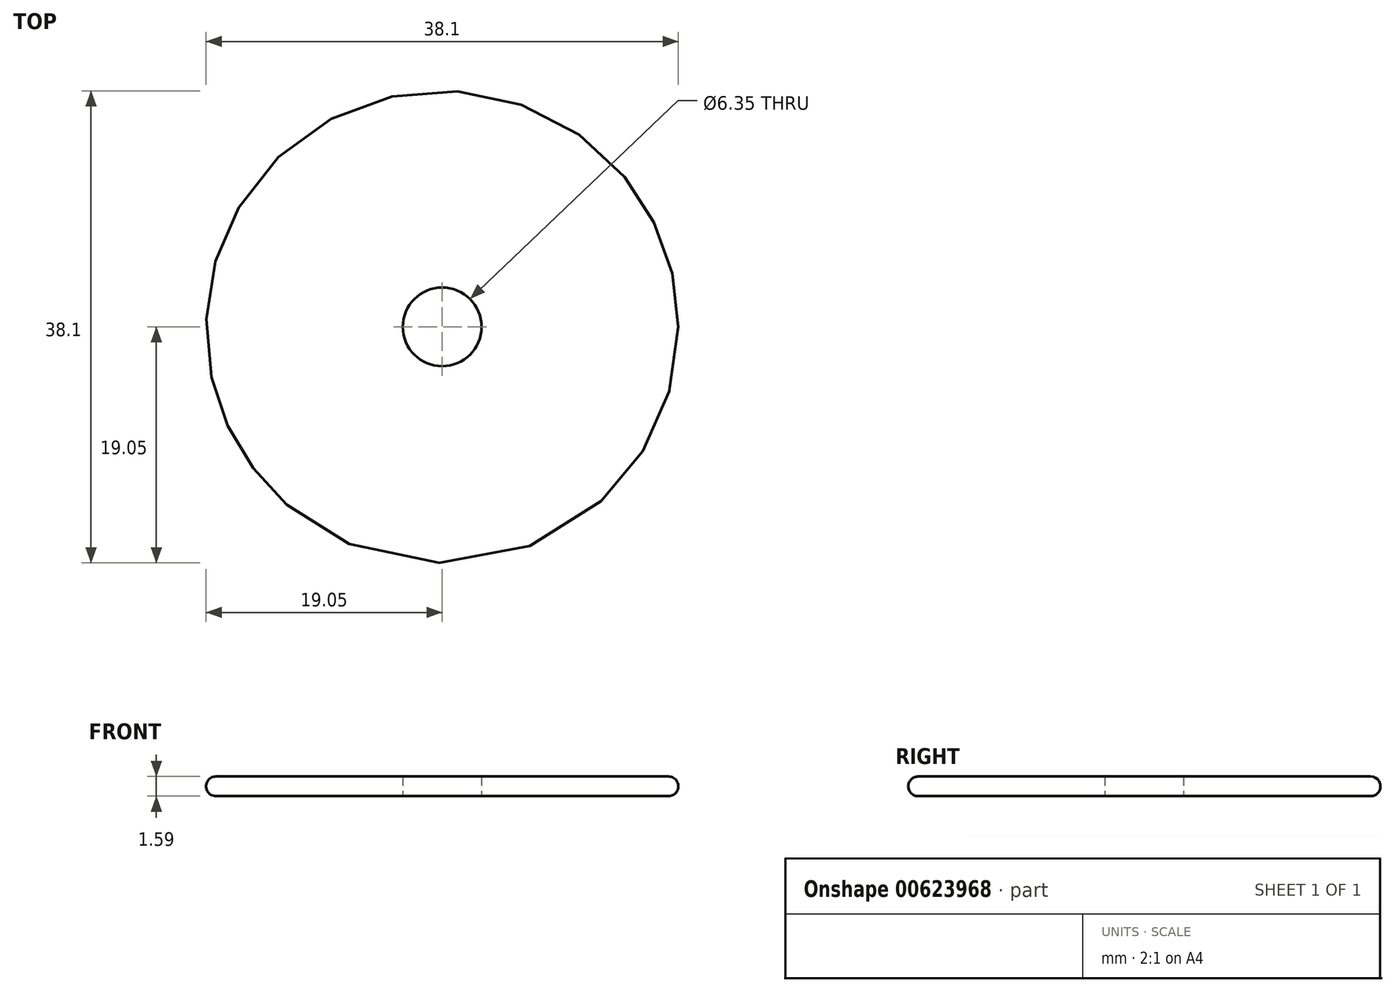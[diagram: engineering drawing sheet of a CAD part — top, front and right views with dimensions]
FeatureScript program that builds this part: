
annotation { "Feature Type Name" : "Feature", "Feature Type Description" : "" }
export const myFeature = defineFeature(function(context is Context, id is Id, definition is map)
    precondition{}
    {
        {
            var Q0;
            Q0=qCreatedBy(makeId("Top.planeOp"),FACE);
            var sketch = newSketch(context, id + "F0", { "sketchPlane" : qUnion([Q0])});
            skCircle(sketch, "E0", {"center": v(0, 0) * mm, "radius": 19.05 * mm});
            skCircle(sketch, "E1", {"center": v(0, 0) * mm, "radius": 3.18 * mm});
            skSolve(sketch);
        }
        {
            var Q0;
            Q0=makeQuery(id+"F0.imprint","IMPRINT",FACE,{"disambiguationData":[TD([[makeQuery(id+"F0.imprint","IMPRINT",EDGE,{"derivedFrom":sQuery(id+"F0.wireOp",EDGE,"E0")}),1.0]])]});
            extrude(context, id + "F1", {"entities" : qUnion([Q0]), "depth" : 1.59 * mm, "offsetDistance" : 25.4 * mm});
        }
        {
            var Q0;
            Q0=makeQuery(id+"F1.opExtrude","SWEPT_FACE",FACE,{"disambiguationData":[OSD([sQuery(id+"F0.wireOp",EDGE,"E0")])]});
            fillet(context, id + "F2", {"entities" : qUnion([Q0]), "radius" : 0.8 * mm, "tangentPropagation" : true, "allowEdgeOverflow" : false});
        }
    });
